# Revit family: BIMLIB_ВытяжныеОсевыеВентиляторы_Вытяжка_AXW-B_SHUFT
name_source: partatom
category: Воздухораспределители
revit_build: Autodesk Revit 2017 (Build: 20170118_1100(x64)
units: mm (PartAtom-declared; Revit-internal decimal feet)

## family parameters
Всегда вертикально = Да
На основе рабочей плоскости = Нет
Общий = Нет
При загрузке вырезать с полостями = Нет
Размер круглого соединителя = Использовать диаметр
Тип детали = Нормальный
Точка расчета площади = Нет

## types (10) — shared parameters
ADSK_URL документации изделия = http://www.shuft.ru
ADSK_URL страницы изделия = http://www.shuft.ru
ADSK_Версия Revit = 2017
ADSK_Версия семейства = v.1
ADSK_Единица измерения = шт.
ADSK_Завод-изготовитель = ООО «Завод ВКО» марка SHUFT
ADSK_Классификация нагрузок = Прочее
ADSK_Коэффициент мощности = 1
ADSK_Материал = BIMLIB_Сталь_SHUFT
BL_BIM library = https://bimlib.pro
IP Двигателя = IP54
URL = http://www.shuft.ru
Изготовитель = ООО «Завод ВКО» марка SHUFT
Климатическое исполнение = У2
Материал сетки = BIMLIB_Сетка_SHUFT

## per-type parameters (varying)
- AXW 550-B-4D: A=725 мм; ADSK_Код изделия=AXW 550-B-4D; ADSK_Количество фаз=3; ADSK_Марка=AXW 550-B-4D; ADSK_Масса=13; ADSK_Наименование=Вытяжной осевой вентилятор AXW 550-B-4D; ADSK_Напряжение=400 В; ADSK_Номинальная мощность=1 кВт; ADSK_Полная мощность=1 кВт; ADSK_Размер_Диаметр=550 мм; ADSK_Ток=1 А; ADSK_Частота вращения вентилятора=1300; B=15 мм; C=115 мм; D1=560 мм; D2=570 мм; D3=137 мм; E=60 мм; F=290 мм; G=20 мм; N=274 мм; r1=280 мм; r2=285 мм; r3=69 мм; Сетка 1=Нет; Сетка 2=Да; Сетка 3=Нет
- AXW 200-B-2E: A=310 мм; ADSK_Код изделия=AXW 200-B-2E; ADSK_Количество фаз=1; ADSK_Марка=AXW 200-B-2E; ADSK_Масса=3.3; ADSK_Наименование=Вытяжной осевой вентилятор AXW 200-B-2E; ADSK_Напряжение=230 В; ADSK_Номинальная мощность=0 кВт; ADSK_Полная мощность=0 кВт; ADSK_Размер_Диаметр=200 мм; ADSK_Ток=0 А; ADSK_Частота вращения вентилятора=2500; B=15 мм; C=68 мм; D1=203 мм; D2=210 мм; D3=92 мм; E=60 мм; F=110 мм; G=25 мм; N=274 мм; r1=102 мм; r2=105 мм; r3=46 мм; Сетка 1=Да; Сетка 2=Нет; Сетка 3=Нет
- AXW 250-B-2E: A=370 мм; ADSK_Код изделия=AXW 250-B-2E; ADSK_Количество фаз=1; ADSK_Марка=AXW 250-B-2E; ADSK_Масса=3.5; ADSK_Наименование=Вытяжной осевой вентилятор AXW 250-B-2E; ADSK_Напряжение=230 В; ADSK_Номинальная мощность=0 кВт; ADSK_Полная мощность=0 кВт; ADSK_Размер_Диаметр=250 мм; ADSK_Ток=0 А; ADSK_Частота вращения вентилятора=2400; B=15 мм; C=90 мм; D1=260 мм; D2=280 мм; D3=92 мм; E=60 мм; F=145 мм; G=25 мм; N=274 мм; r1=130 мм; r2=140 мм; r3=46 мм; Сетка 1=Да; Сетка 2=Нет; Сетка 3=Нет
- AXW 300-B-4E: A=430 мм; ADSK_Код изделия=AXW 300-B-2E; ADSK_Количество фаз=1; ADSK_Марка=AXW 300-B-2E; ADSK_Масса=4; ADSK_Наименование=Вытяжной осевой вентилятор AXW 300-B-2E; ADSK_Напряжение=230 В; ADSK_Номинальная мощность=0 кВт; ADSK_Полная мощность=0 кВт; ADSK_Размер_Диаметр=300 мм; ADSK_Ток=0 А; ADSK_Частота вращения вентилятора=1380; B=15 мм; C=90 мм; D1=315 мм; D2=335 мм; D3=92 мм; E=60 мм; F=173 мм; G=25 мм; N=274 мм; r1=158 мм; r2=168 мм; r3=46 мм; Сетка 1=Да; Сетка 2=Нет; Сетка 3=Нет
- AXW 350-B-4E: A=485 мм; ADSK_Код изделия=AXW 350-B-4E; ADSK_Количество фаз=1; ADSK_Марка=AXW 350-B-4E; ADSK_Масса=6; ADSK_Наименование=Вытяжной осевой вентилятор AXW 350-B-4E; ADSK_Напряжение=230 В; ADSK_Номинальная мощность=0 кВт; ADSK_Полная мощность=0 кВт; ADSK_Размер_Диаметр=350 мм; ADSK_Ток=1 А; ADSK_Частота вращения вентилятора=1400; B=15 мм; C=110 мм; D1=360 мм; D2=380 мм; D3=102 мм; E=60 мм; F=195 мм; G=10 мм; N=165 мм; r1=180 мм; r2=190 мм; r3=51 мм; Сетка 1=Нет; Сетка 2=Да; Сетка 3=Нет
- AXW 400-B-4E: A=540 мм; ADSK_Код изделия=AXW 400-B-4E; ADSK_Количество фаз=1; ADSK_Марка=AXW 400-B-4E; ADSK_Масса=7; ADSK_Наименование=Вытяжной осевой вентилятор AXW 400-B-4E; ADSK_Напряжение=230 В; ADSK_Номинальная мощность=0 кВт; ADSK_Полная мощность=0 кВт; ADSK_Размер_Диаметр=400 мм; ADSK_Ток=1 А; ADSK_Частота вращения вентилятора=1380; B=15 мм; C=110 мм; D1=410 мм; D2=430 мм; D3=102 мм; E=60 мм; F=220 мм; G=20 мм; N=200 мм; r1=205 мм; r2=215 мм; r3=51 мм; Сетка 1=Нет; Сетка 2=Да; Сетка 3=Нет
- AXW 450-B-4E: A=575 мм; ADSK_Код изделия=AXW 450-B-4E; ADSK_Количество фаз=1; ADSK_Марка=AXW 450-B-4E; ADSK_Масса=9; ADSK_Наименование=Вытяжной осевой вентилятор AXW 450-B-4E; ADSK_Напряжение=230 В; ADSK_Номинальная мощность=0 кВт; ADSK_Полная мощность=0 кВт; ADSK_Размер_Диаметр=450 мм; ADSK_Ток=1 А; ADSK_Частота вращения вентилятора=1350; B=15 мм; C=110 мм; D1=460 мм; D2=480 мм; D3=102 мм; E=60 мм; F=245 мм; G=20 мм; N=225 мм; r1=230 мм; r2=240 мм; r3=51 мм; Сетка 1=Нет; Сетка 2=Да; Сетка 3=Нет
- AXW 630-B-4D: A=805 мм; ADSK_Код изделия=AXW 630-B-4D; ADSK_Количество фаз=3; ADSK_Марка=AXW 630-B-4D; ADSK_Масса=17; ADSK_Наименование=Вытяжной осевой вентилятор AXW 630-B-4D; ADSK_Напряжение=400 В; ADSK_Номинальная мощность=1 кВт; ADSK_Полная мощность=1 кВт; ADSK_Размер_Диаметр=630 мм; ADSK_Ток=2 А; ADSK_Частота вращения вентилятора=1320; B=15 мм; C=125 мм; D1=640 мм; D2=660 мм; D3=137 мм; E=60 мм; F=335 мм; G=20 мм; N=315 мм; r1=320 мм; r2=330 мм; r3=69 мм; Сетка 1=Нет; Сетка 2=Да; Сетка 3=Нет
- AXW 760-B-6D 0.65кВТ: A=845 мм; ADSK_Код изделия=AXW 760-B-6D; ADSK_Количество фаз=3; ADSK_Марка=AXW 760-B-6D; ADSK_Масса=40; ADSK_Наименование=Вытяжной осевой вентилятор AXW 760-B-6D; ADSK_Напряжение=400 В; ADSK_Номинальная мощность=1 кВт; ADSK_Полная мощность=1 кВт; ADSK_Размер_Диаметр=760 мм; ADSK_Ток=1 А; ADSK_Частота вращения вентилятора=730; B=27 мм; C=135 мм; D1=705 мм; D2=718 мм; D3=180 мм; E=130 мм; F=364 мм; G=20 мм; N=315 мм; r1=353 мм; r2=359 мм; r3=90 мм; Сетка 1=Нет; Сетка 2=Нет; Сетка 3=Да
- AXW 760-B-6D 0.9кВт: A=845 мм; ADSK_Код изделия=AXW 760-B-6D; ADSK_Количество фаз=3; ADSK_Марка=AXW 760-B-6D; ADSK_Масса=40; ADSK_Наименование=Вытяжной осевой вентилятор AXW 760-B-6D; ADSK_Напряжение=400 В; ADSK_Номинальная мощность=1 кВт; ADSK_Полная мощность=1 кВт; ADSK_Размер_Диаметр=760 мм; ADSK_Ток=2 А; ADSK_Частота вращения вентилятора=900; B=27 мм; C=135 мм; D1=705 мм; D2=718 мм; D3=180 мм; E=130 мм; F=364 мм; G=20 мм; N=315 мм; r1=353 мм; r2=359 мм; r3=90 мм; Сетка 1=Нет; Сетка 2=Нет; Сетка 3=Да
